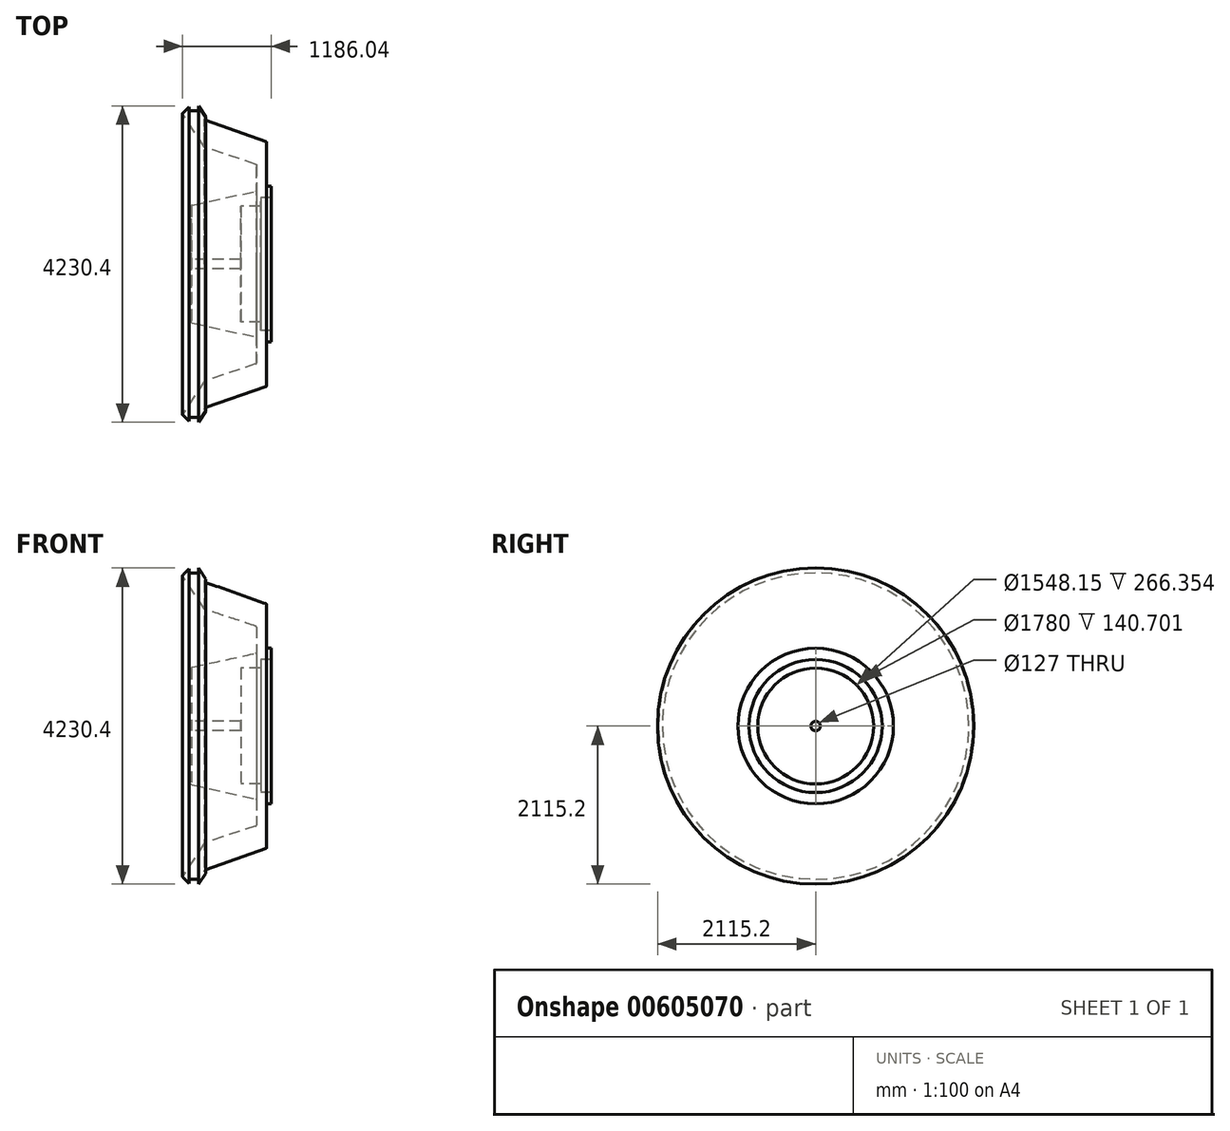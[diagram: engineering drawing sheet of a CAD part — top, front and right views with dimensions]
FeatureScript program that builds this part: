
annotation { "Feature Type Name" : "Feature", "Feature Type Description" : "" }
export const myFeature = defineFeature(function(context is Context, id is Id, definition is map)
    precondition{}
    {
        {
            var Q0;
            Q0=qCreatedBy(makeId("Front.planeOp"),FACE);
            var sketch = newSketch(context, id + "F0", { "sketchPlane" : qUnion([Q0])});
            skLineSegment(sketch, "E0", {"start": v(-660.4, 0) * mm, "end": v(-660.4, 775.42) * mm});
            skLineSegment(sketch, "E1", {"start": v(-650.41, 787.83) * mm, "end": v(199.63, 973.77) * mm});
            skLineSegment(sketch, "E2", {"start": v(209.62, 986.17) * mm, "end": v(209.62, 1323.42) * mm});
            skLineSegment(sketch, "E3", {"start": v(200.94, 1335.46) * mm, "end": v(-483.92, 1563.75) * mm});
            skLineSegment(sketch, "E4", {"start": v(-490.53, 1568.84) * mm, "end": v(-776.9, 2005.94) * mm});
            skLineSegment(sketch, "E5", {"start": v(-775.04, 2022.1) * mm, "end": v(-688.74, 2104.24) * mm});
            skLineSegment(sketch, "E6", {"start": v(-688.74, 2104.24) * mm, "end": v(-688.74, 2049.42) * mm});
            skLineSegment(sketch, "E7", {"start": v(-688.74, 2049.42) * mm, "end": v(-565.98, 2049.42) * mm});
            skLineSegment(sketch, "E8", {"start": v(-565.98, 2049.42) * mm, "end": v(-565.98, 2115.2) * mm});
            skLineSegment(sketch, "E9", {"start": v(-565.98, 2115.2) * mm, "end": v(-471.34, 1970.75) * mm});
            skLineSegment(sketch, "E10", {"start": v(-475, 1953.17) * mm, "end": v(-483.57, 1947.56) * mm});
            skLineSegment(sketch, "E11", {"start": v(-480.83, 1924.96) * mm, "end": v(337.03, 1637.03) * mm});
            skLineSegment(sketch, "E12", {"start": v(345.51, 1625.05) * mm, "end": v(345.51, 1040.24) * mm});
            skLineSegment(sketch, "E13", {"start": v(345.51, 1040.24) * mm, "end": v(407.06, 1040.24) * mm});
            skLineSegment(sketch, "E14", {"start": v(407.06, 1040.24) * mm, "end": v(407.06, 890) * mm});
            skLineSegment(sketch, "E15", {"start": v(407.06, 890) * mm, "end": v(266.35, 890) * mm});
            skLineSegment(sketch, "E16", {"start": v(266.35, 890) * mm, "end": v(266.35, 774.08) * mm});
            skLineSegment(sketch, "E17", {"start": v(266.35, 774.08) * mm, "end": v(0, 774.08) * mm});
            skLineSegment(sketch, "E18", {"start": v(0, 774.08) * mm, "end": v(0, 0) * mm});
            skLineSegment(sketch, "E19", {"start": v(-660.4, 0) * mm, "end": v(0, 0) * mm});
            skPoint(sketch, "E20.visualSharp", {"position": v(345.51, 1634.04) * mm});
            skArc(sketch, "E20.filletArc", {"start": v(345.51, 1625.05) * mm, "mid": v(343.18, 1632.4) * mm, "end": v(337.03, 1637.03) * mm});
            skPoint(sketch, "E21.visualSharp", {"position": v(-505.05, 1933.48) * mm});
            skArc(sketch, "E21.filletArc", {"start": v(-483.57, 1947.56) * mm, "mid": v(-489.22, 1935.4) * mm, "end": v(-480.83, 1924.96) * mm});
            skPoint(sketch, "E22.visualSharp", {"position": v(-464.38, 1960.13) * mm});
            skArc(sketch, "E22.filletArc", {"start": v(-475, 1953.17) * mm, "mid": v(-469.53, 1961.2) * mm, "end": v(-471.34, 1970.75) * mm});
            skPoint(sketch, "E23.visualSharp", {"position": v(-782.71, 2014.8) * mm});
            skArc(sketch, "E23.filletArc", {"start": v(-775.04, 2022.1) * mm, "mid": v(-778.9, 2014.36) * mm, "end": v(-776.9, 2005.94) * mm});
            skPoint(sketch, "E24.visualSharp", {"position": v(-488.11, 1565.15) * mm});
            skArc(sketch, "E24.filletArc", {"start": v(-490.53, 1568.84) * mm, "mid": v(-487.66, 1565.74) * mm, "end": v(-483.92, 1563.75) * mm});
            skPoint(sketch, "E25.visualSharp", {"position": v(209.62, 1332.57) * mm});
            skArc(sketch, "E25.filletArc", {"start": v(209.62, 1323.42) * mm, "mid": v(207.22, 1330.84) * mm, "end": v(200.94, 1335.46) * mm});
            skPoint(sketch, "E26.visualSharp", {"position": v(209.62, 975.95) * mm});
            skArc(sketch, "E26.filletArc", {"start": v(199.63, 973.77) * mm, "mid": v(206.81, 978.2) * mm, "end": v(209.62, 986.17) * mm});
            skPoint(sketch, "E27.visualSharp", {"position": v(-660.4, 785.65) * mm});
            skArc(sketch, "E27.filletArc", {"start": v(-650.41, 787.83) * mm, "mid": v(-657.6, 783.39) * mm, "end": v(-660.4, 775.42) * mm});
            skSolve(sketch);
        }
        {
            var Q0;
            Q0=makeQuery(id+"F0.imprint","IMPRINT",FACE,{"disambiguationData":[TD([[makeQuery(id+"F0.imprint","IMPRINT",EDGE,{"derivedFrom":sQuery(id+"F0.wireOp",EDGE,"E0")}),-1.0]])]});
            var Q1;
            Q1=sQuery(id+"F0.wireOp",EDGE,"E19");
            revolve(context, id + "F1", {"entities" : qUnion([Q0]), "axis" : qUnion([Q1]), "revolveType" : RevolveType.FULL});
        }
        {
            var Q0;
            Q0=makeQuery(id+"F1.opRevolve","SWEPT_FACE",FACE,{"disambiguationData":[OSD([sQuery(id+"F0.wireOp",EDGE,"E0")])]});
            var sketch = newSketch(context, id + "F2", { "sketchPlane" : qUnion([Q0])});
            skCircle(sketch, "E28", {"center": v(0, 0) * mm, "radius": 782.14 * mm});
            skSolve(sketch);
        }
        {
            var Q0;
            Q0=sQuery(id+"F2.wireOp",VERTEX,"E28.center");
            var Q1;
            Q1=makeQuery(id+"F1.opRevolve","SWEPT_BODY",BODY,{"disambiguationData":[OSD([sQuery(id+"F0.wireOp",EDGE,"E0"),sQuery(id+"F0.wireOp",EDGE,"E1"),sQuery(id+"F0.wireOp",EDGE,"E2"),sQuery(id+"F0.wireOp",EDGE,"E3"),sQuery(id+"F0.wireOp",EDGE,"E4"),sQuery(id+"F0.wireOp",EDGE,"E5"),sQuery(id+"F0.wireOp",EDGE,"E6"),sQuery(id+"F0.wireOp",EDGE,"E7"),sQuery(id+"F0.wireOp",EDGE,"E8"),sQuery(id+"F0.wireOp",EDGE,"E9"),sQuery(id+"F0.wireOp",EDGE,"E10"),sQuery(id+"F0.wireOp",EDGE,"E11"),sQuery(id+"F0.wireOp",EDGE,"E12"),sQuery(id+"F0.wireOp",EDGE,"E13"),sQuery(id+"F0.wireOp",EDGE,"E14"),sQuery(id+"F0.wireOp",EDGE,"E15"),sQuery(id+"F0.wireOp",EDGE,"E16"),sQuery(id+"F0.wireOp",EDGE,"E17"),sQuery(id+"F0.wireOp",EDGE,"E18"),sQuery(id+"F0.wireOp",EDGE,"E19"),sQuery(id+"F0.wireOp",EDGE,"E20.filletArc"),sQuery(id+"F0.wireOp",EDGE,"E21.filletArc"),sQuery(id+"F0.wireOp",EDGE,"E22.filletArc"),sQuery(id+"F0.wireOp",EDGE,"E23.filletArc"),sQuery(id+"F0.wireOp",EDGE,"E24.filletArc"),sQuery(id+"F0.wireOp",EDGE,"E25.filletArc"),sQuery(id+"F0.wireOp",EDGE,"E26.filletArc"),sQuery(id+"F0.wireOp",EDGE,"E27.filletArc")])]});
            hole(context, id + "F3", {"style" : HoleStyle.SIMPLE, "endStyle" : HoleEndStyle.THROUGH, "standardTappedOrClearance" : lookupTablePath({ "standard" : "Custom", "fit" : "Normal", "size" : "1/4", "type" : "Clearance" }), "standardBlindInLast" : lookupTablePath({ "fit" : "Free", "standard" : "Custom", "size" : "1/4", "type" : "Clearance" }), "holeDiameter" : 127 * mm, "majorDiameter" : 5 * mm, "isTappedThrough" : true, "tappedDepth" : 12 * mm, "tapClearance" : 3, "locations" : qUnion([Q0]), "scope" : qUnion([Q1])});
        }
    });
